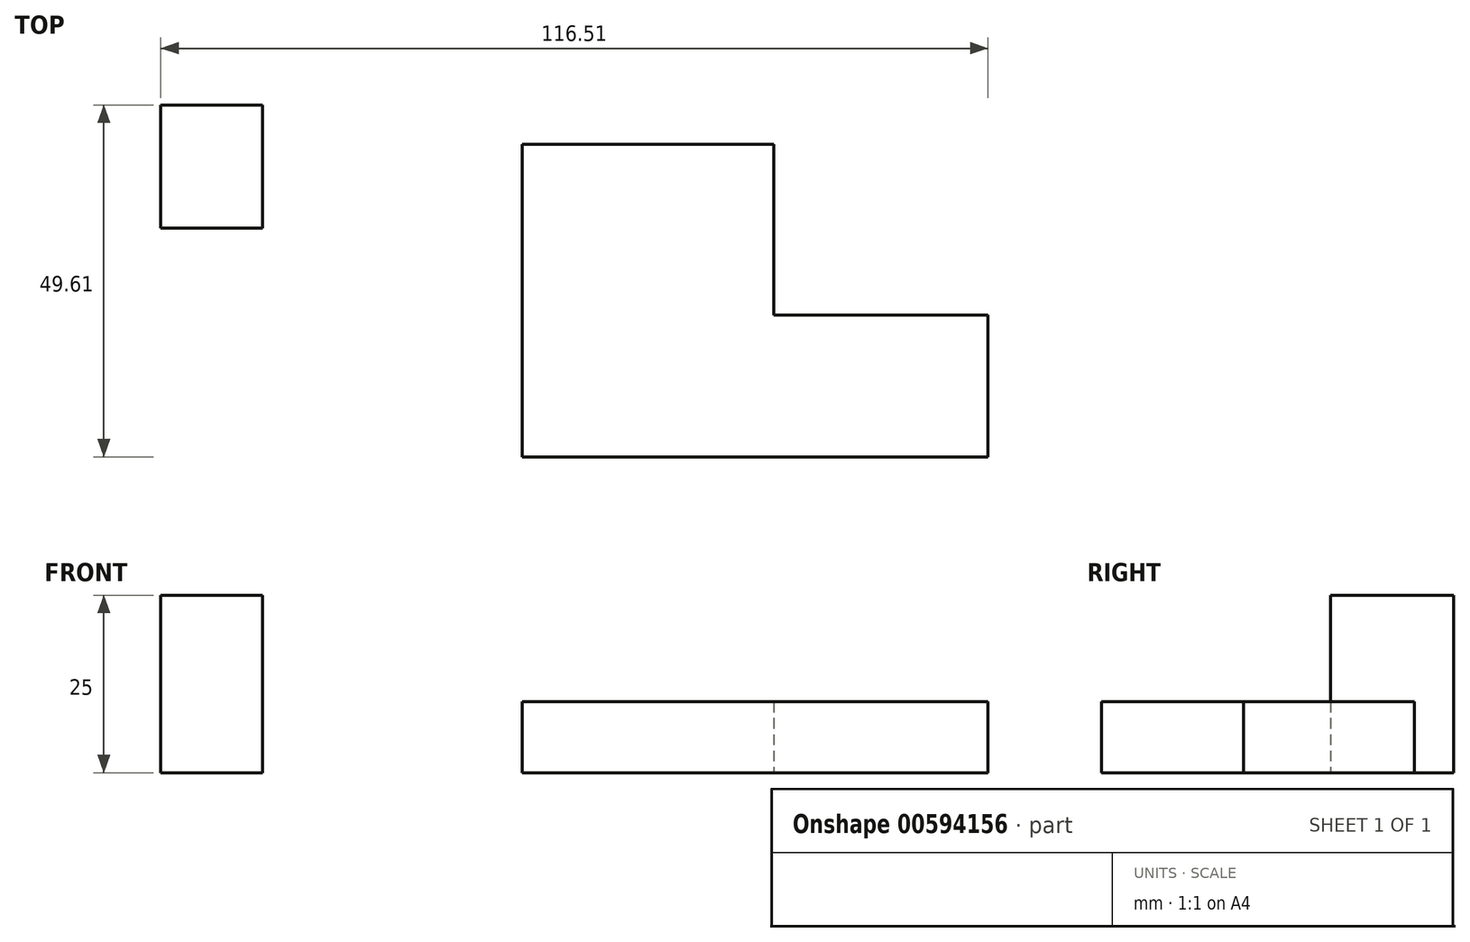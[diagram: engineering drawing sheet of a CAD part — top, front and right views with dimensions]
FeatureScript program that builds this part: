
annotation { "Feature Type Name" : "Feature", "Feature Type Description" : "" }
export const myFeature = defineFeature(function(context is Context, id is Id, definition is map)
    precondition{}
    {
        {
            var Q0;
            Q0=qCreatedBy(makeId("Top.planeOp"),FACE);
            var sketch = newSketch(context, id + "F0", { "sketchPlane" : qUnion([Q0])});
            skLineSegment(sketch, "E0", {"start": v(0, 0) * mm, "end": v(0, 44.07) * mm});
            skLineSegment(sketch, "E1", {"start": v(0, 44.07) * mm, "end": v(35.42, 44.07) * mm});
            skLineSegment(sketch, "E2", {"start": v(35.42, 44.07) * mm, "end": v(35.42, 20) * mm});
            skLineSegment(sketch, "E3", {"start": v(35.42, 20) * mm, "end": v(65.6, 20) * mm});
            skLineSegment(sketch, "E4", {"start": v(65.6, 0) * mm, "end": v(0, 0) * mm});
            skLineSegment(sketch, "E5", {"start": v(65.6, 20) * mm, "end": v(65.6, 0) * mm});
            skSolve(sketch);
        }
        {
            var Q0;
            Q0=qCreatedBy(makeId("Top.planeOp"),FACE);
            var sketch = newSketch(context, id + "F1", { "sketchPlane" : qUnion([Q0])});
            skSolve(sketch);
        }
        {
            var Q0;
            Q0 = qSketchRegion(id + "F1", true);
            var Q1;
            Q1=makeQuery(id+"F0.imprint","IMPRINT",FACE,{"disambiguationData":[TD([[makeQuery(id+"F0.imprint","IMPRINT",EDGE,{"derivedFrom":sQuery(id+"F0.wireOp",EDGE,"E0")}),-1.0]])]});
            extrude(context, id + "F2", {"entities" : qUnion([Q0, Q1]), "depth" : 10 * mm, "offsetDistance" : 25 * mm});
        }
        {
            var Q0;
            Q0=qCreatedBy(makeId("Top.planeOp"),FACE);
            var sketch = newSketch(context, id + "F3", { "sketchPlane" : qUnion([Q0])});
            skLineSegment(sketch, "E6.bottom", {"start": v(-50.92, 49.6) * mm, "end": v(-36.6, 49.6) * mm});
            skLineSegment(sketch, "E6.top", {"start": v(-50.92, 32.27) * mm, "end": v(-36.6, 32.27) * mm});
            skLineSegment(sketch, "E6.left", {"start": v(-50.92, 49.6) * mm, "end": v(-50.92, 32.27) * mm});
            skLineSegment(sketch, "E6.right", {"start": v(-36.6, 49.6) * mm, "end": v(-36.6, 32.27) * mm});
            skSolve(sketch);
        }
        {
            var Q0;
            Q0 = qSketchRegion(id + "FuScD1Fm61FnSY6_1", true);
            var Q1;
            Q1=makeQuery(id+"F3.imprint","IMPRINT",FACE,{"disambiguationData":[TD([[makeQuery(id+"F3.imprint","IMPRINT",EDGE,{"derivedFrom":sQuery(id+"F3.wireOp",EDGE,"E6.bottom")}),-1.0]])]});
            extrude(context, id + "F4", {"entities" : qUnion([Q0, Q1]), "depth" : 25 * mm, "offsetDistance" : 25 * mm});
        }
    });
